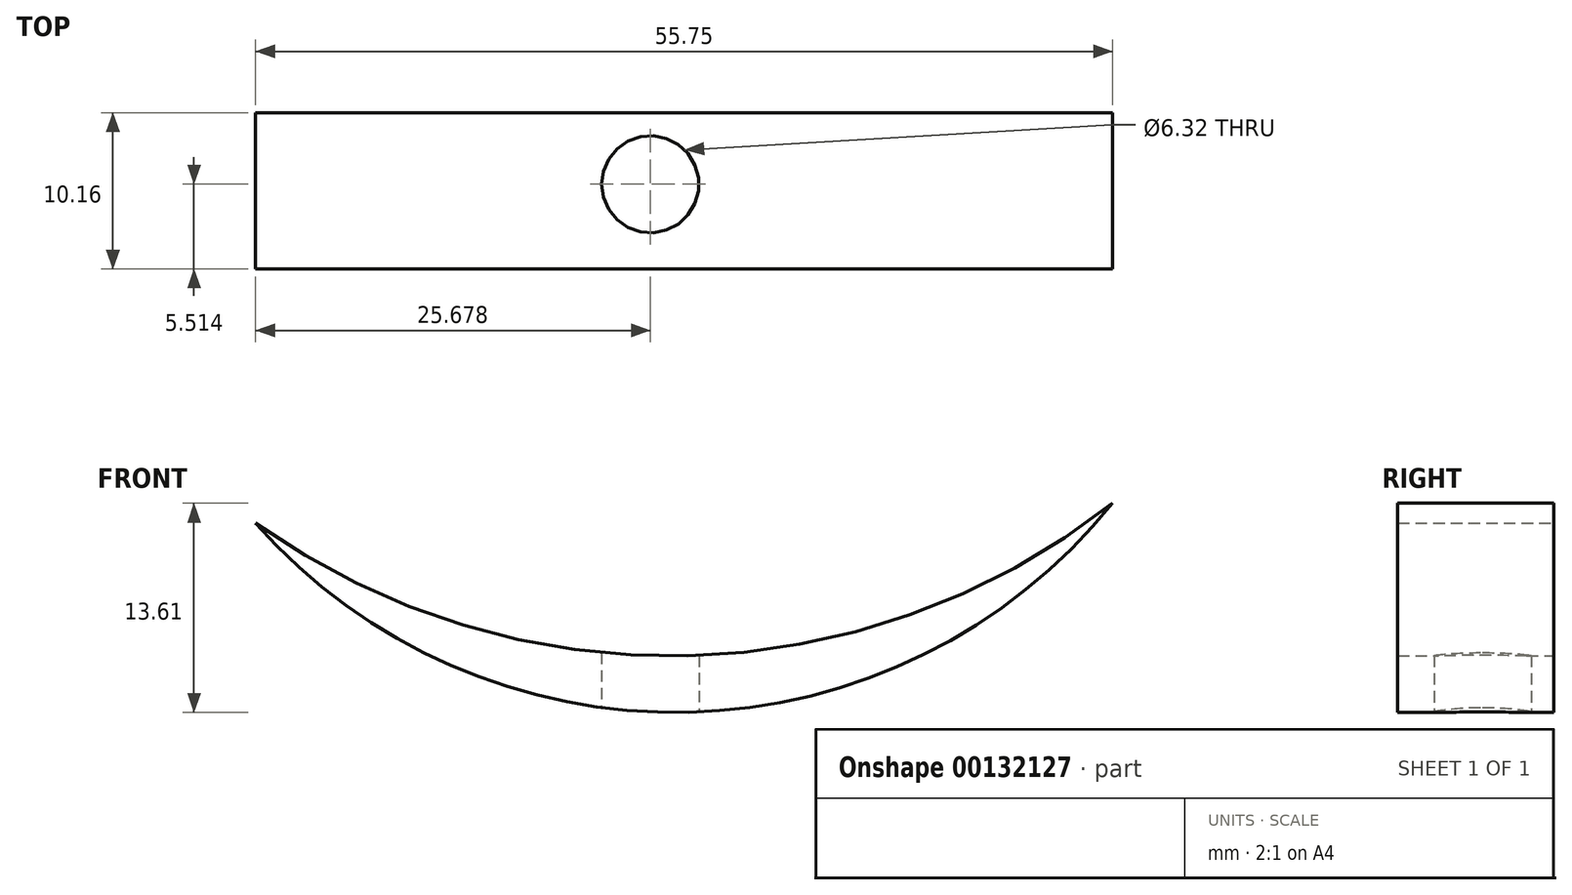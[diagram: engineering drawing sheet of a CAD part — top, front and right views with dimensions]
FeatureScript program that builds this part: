
annotation { "Feature Type Name" : "Feature", "Feature Type Description" : "" }
export const myFeature = defineFeature(function(context is Context, id is Id, definition is map)
    precondition{}
    {
        {
            var Q0;
            Q0=qCreatedBy(makeId("Front.planeOp"),FACE);
            var sketch = newSketch(context, id + "F0", { "sketchPlane" : qUnion([Q0])});
            skArc(sketch, "E0", {"start": v(-63.36, 37.68) * mm, "mid": v(-35.19, 25.37) * mm, "end": v(-7.61, 38.97) * mm});
            skArc(sketch, "E1", {"start": v(-63.36, 37.68) * mm, "mid": v(-35.27, 29.05) * mm, "end": v(-7.61, 38.97) * mm});
            skSolve(sketch);
        }
        {
            var Q0;
            Q0 = qSketchRegion(id + "F0", true);
            extrude(context, id + "F1", {"entities" : qUnion([Q0]), "depth" : 10.16 * mm});
        }
        {
            var Q0;
            Q0=qCreatedBy(makeId("Top.planeOp"),FACE);
            var sketch = newSketch(context, id + "F2", { "sketchPlane" : qUnion([Q0])});
            skCircle(sketch, "E2", {"center": v(-37.68, -4.65) * mm, "radius": 3.16 * mm});
            skSolve(sketch);
        }
        {
            var Q0;
            Q0 = qSketchRegion(id + "F2", true);
            extrude(context, id + "F3", {"entities" : qUnion([Q0]), "operationType" : NewBodyOperationType.REMOVE, "depth" : 127 * mm});
        }
    });
